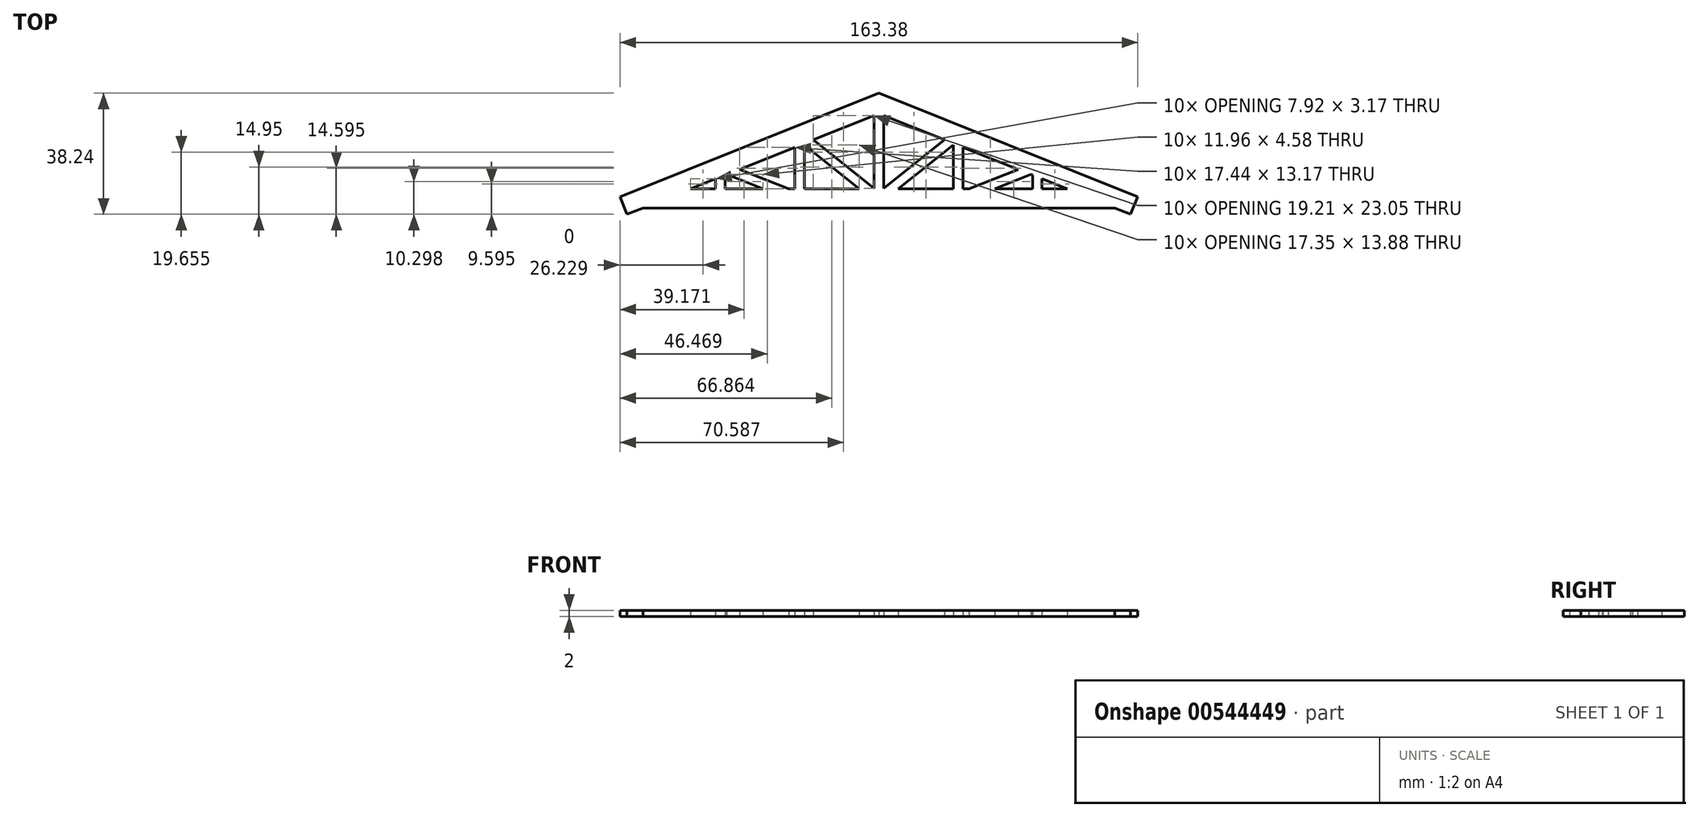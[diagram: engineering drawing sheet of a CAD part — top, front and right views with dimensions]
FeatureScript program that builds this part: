
annotation { "Feature Type Name" : "Feature", "Feature Type Description" : "" }
export const myFeature = defineFeature(function(context is Context, id is Id, definition is map)
    precondition{}
    {
        {
            var Q0;
            Q0=qCreatedBy(makeId("Top.planeOp"),FACE);
            var sketch = newSketch(context, id + "F0", { "sketchPlane" : qUnion([Q0])});
            skPoint(sketch, "E0", {"position": v(25, 0) * mm});
            skPoint(sketch, "E1", {"position": v(50, 0) * mm});
            skPoint(sketch, "E2.MirrorP", {"position": v(-25, 0) * mm});
            skPoint(sketch, "E3.MirrorP", {"position": v(-50, 0) * mm});
            skLineSegment(sketch, "E4.0", {"start": v(0, 33.23) * mm, "end": v(-76.11, 2.79) * mm});
            skLineSegment(sketch, "E5.0", {"start": v(0, 33.23) * mm, "end": v(76.11, 2.79) * mm});
            skLineSegment(sketch, "E6.MirrorCS", {"start": v(-1.5, 26.17) * mm, "end": v(-20.7, 18.49) * mm});
            skLineSegment(sketch, "E7.MirrorCS", {"start": v(1.5, 26.17) * mm, "end": v(20.7, 18.49) * mm});
            skPoint(sketch, "E8.orphan", {"position": v(-2.23, 27.66) * mm});
            skPoint(sketch, "E9.orphan", {"position": v(2.23, 27.66) * mm});
            skLineSegment(sketch, "E10.0", {"start": v(-76.11, 2.79) * mm, "end": v(-81.69, 0.56) * mm});
            skLineSegment(sketch, "E11.0", {"start": v(76.11, 2.79) * mm, "end": v(81.69, 0.56) * mm});
            skLineSegment(sketch, "E12.MirrorCS", {"start": v(-74.42, -3) * mm, "end": v(-79.46, -5.01) * mm});
            skLineSegment(sketch, "E13.MirrorCS", {"start": v(74.42, -3) * mm, "end": v(79.46, -5.01) * mm});
            skLineSegment(sketch, "E14", {"start": v(-81.69, 0.56) * mm, "end": v(-79.46, -5.01) * mm});
            skLineSegment(sketch, "E15", {"start": v(79.46, -5.01) * mm, "end": v(81.69, 0.56) * mm});
            skLineSegment(sketch, "E16.0", {"start": v(-51.5, 3) * mm, "end": v(-51.5, 6.17) * mm});
            skLineSegment(sketch, "E17.MirrorCS", {"start": v(-48.5, 3) * mm, "end": v(-48.5, 7.37) * mm});
            skPoint(sketch, "E18.orphan", {"position": v(-51.5, 7.37) * mm});
            skLineSegment(sketch, "E19.MirrorCS", {"start": v(48.5, 3) * mm, "end": v(48.5, 7.37) * mm});
            skLineSegment(sketch, "E20.MirrorCS", {"start": v(51.5, 3) * mm, "end": v(51.5, 6.17) * mm});
            skLineSegment(sketch, "E21.0", {"start": v(-23.5, 3) * mm, "end": v(-23.5, 16.77) * mm});
            skLineSegment(sketch, "E21.1", {"start": v(-46.52, 7) * mm, "end": v(-36.54, 3) * mm});
            skLineSegment(sketch, "E22.0", {"start": v(-26.5, 3) * mm, "end": v(-26.5, 16.17) * mm});
            skLineSegment(sketch, "E22.1", {"start": v(-43.94, 9.2) * mm, "end": v(-28.46, 3) * mm});
            skLineSegment(sketch, "E23", {"start": v(-23.5, 16.77) * mm, "end": v(-23.5, 16.88) * mm});
            skLineSegment(sketch, "E24", {"start": v(-46.52, 7) * mm, "end": v(-47.98, 7.58) * mm});
            skLineSegment(sketch, "E25.0", {"start": v(-1.5, 3.12) * mm, "end": v(-1.5, 26.17) * mm});
            skLineSegment(sketch, "E25.1", {"start": v(-20.7, 18.49) * mm, "end": v(-1.5, 3.12) * mm});
            skLineSegment(sketch, "E26.0", {"start": v(-23.24, 16.67) * mm, "end": v(-6.15, 3) * mm});
            skLineSegment(sketch, "E27", {"start": v(-23.24, 16.67) * mm, "end": v(-23.5, 16.88) * mm});
            skLineSegment(sketch, "E28.MirrorCS", {"start": v(1.5, 3.12) * mm, "end": v(1.5, 26.17) * mm});
            skLineSegment(sketch, "E29.MirrorCS", {"start": v(20.7, 18.49) * mm, "end": v(1.5, 3.12) * mm});
            skLineSegment(sketch, "E30.MirrorCS", {"start": v(23.24, 16.67) * mm, "end": v(6.15, 3) * mm});
            skLineSegment(sketch, "E31.MirrorCS", {"start": v(23.5, 3) * mm, "end": v(23.5, 16.77) * mm});
            skLineSegment(sketch, "E32.MirrorCS", {"start": v(26.5, 3) * mm, "end": v(26.5, 16.17) * mm});
            skLineSegment(sketch, "E33.MirrorCS", {"start": v(43.94, 9.2) * mm, "end": v(28.46, 3) * mm});
            skLineSegment(sketch, "E34.MirrorCS", {"start": v(46.52, 7) * mm, "end": v(36.54, 3) * mm});
            skLineSegment(sketch, "E35.MirrorCS", {"start": v(46.52, 7) * mm, "end": v(47.98, 7.58) * mm});
            skLineSegment(sketch, "E36.MirrorCS", {"start": v(23.24, 16.67) * mm, "end": v(23.5, 16.88) * mm});
            skLineSegment(sketch, "E37.MirrorCS", {"start": v(23.5, 16.77) * mm, "end": v(23.5, 16.88) * mm});
            skPoint(sketch, "E38.orphan", {"position": v(1.5, 30) * mm});
            skPoint(sketch, "E39.orphan", {"position": v(-1.5, 30) * mm});
            skPoint(sketch, "E40.orphan", {"position": v(-75, 0) * mm});
            skLineSegment(sketch, "E41.0", {"start": v(-66.92, -3) * mm, "end": v(66.92, -3) * mm});
            skLineSegment(sketch, "E42", {"start": v(-66.92, -3) * mm, "end": v(-74.42, -3) * mm});
            skLineSegment(sketch, "E43", {"start": v(66.92, -3) * mm, "end": v(74.42, -3) * mm});
            skLineSegment(sketch, "E44.0", {"start": v(-59.42, 3) * mm, "end": v(-51.5, 3) * mm});
            skPoint(sketch, "E45.orphan", {"position": v(-48.5, 0) * mm});
            skPoint(sketch, "E46.orphan", {"position": v(-51.5, 0) * mm});
            skPoint(sketch, "E47.orphan", {"position": v(-29.04, 0) * mm});
            skPoint(sketch, "E48.orphan", {"position": v(-26.5, 2.22) * mm});
            skPoint(sketch, "E49.orphan", {"position": v(-23.5, 0) * mm});
            skPoint(sketch, "E50.orphan", {"position": v(-2.4, 0) * mm});
            skPoint(sketch, "E51.orphan", {"position": v(2.4, 0) * mm});
            skPoint(sketch, "E52.orphan", {"position": v(23.5, 0) * mm});
            skPoint(sketch, "E53.orphan", {"position": v(26.5, 2.22) * mm});
            skPoint(sketch, "E54.orphan", {"position": v(29.04, 0) * mm});
            skPoint(sketch, "E55.orphan", {"position": v(48.5, 0) * mm});
            skPoint(sketch, "E56.orphan", {"position": v(51.5, 0) * mm});
            skPoint(sketch, "E57.start.orphan", {"position": v(0, 0) * mm});
            skLineSegment(sketch, "E58.trimOffspring", {"start": v(-47.98, 7.58) * mm, "end": v(-48.5, 7.37) * mm});
            skLineSegment(sketch, "E59.trimOffspring", {"start": v(-51.5, 6.17) * mm, "end": v(-59.42, 3) * mm});
            skLineSegment(sketch, "E60.trimOffspring", {"start": v(-26.5, 16.17) * mm, "end": v(-43.94, 9.2) * mm});
            skLineSegment(sketch, "E61.trimOffspring", {"start": v(-48.5, 3) * mm, "end": v(-36.54, 3) * mm});
            skLineSegment(sketch, "E62.trimOffspring", {"start": v(-28.46, 3) * mm, "end": v(-26.5, 3) * mm});
            skLineSegment(sketch, "E63.trimOffspring", {"start": v(-23.5, 3) * mm, "end": v(-6.15, 3) * mm});
            skLineSegment(sketch, "E64.trimOffspring", {"start": v(6.15, 3) * mm, "end": v(59.42, 3) * mm});
            skLineSegment(sketch, "E65.trimOffspring", {"start": v(26.5, 16.17) * mm, "end": v(43.94, 9.2) * mm});
            skLineSegment(sketch, "E66.trimOffspring", {"start": v(47.98, 7.58) * mm, "end": v(48.5, 7.37) * mm});
            skLineSegment(sketch, "E67.trimOffspring", {"start": v(51.5, 6.17) * mm, "end": v(59.42, 3) * mm});
            skSolve(sketch);
        }
        {
            var Q0;
            Q0 = qSketchRegion(id + "F0", true);
            extrude(context, id + "F1", {"entities" : qUnion([Q0]), "depth" : 2 * mm, "offsetDistance" : 25 * mm});
        }
    });
